# Revit family: Sink-Kitchen-KOHLER-Undertone-K-3188
name_source: partatom
category: Plumbing Fixtures
revit_build: Autodesk Revit 2015 (Build: 20140606_1530(x64)
units: mm (PartAtom-declared; Revit-internal decimal feet)

## types (1)
- NA-Stainless
    ADA Compliant = No
    Assembly Code = D2010400
    Date Modified = 09/19/2017
    Default Elevation = 35"
    Description = Undertone 43inch x 8-1/4inch x 6-5/16inch under-mount single-bowl trough kitchen sink
    Finish = Kohler-Metal-NA-Stainless
    Flow Rate = 0 GPM
    Height = 8 7/8"
    Inlet Connector = Inlet Connection
    Length = 43"
    Manufacturer = KOHLER Co.
    MasterFormat 1995 = 15410
    MasterFormat 2004 = 22.41.16
    Material = 16-Gauge Stainless Steel
    Model = K-3188-NA
    Outlet Connector = Outlet Connection
    Pressure = 0.00 psi
    Product Documentation Link = http://www.us.kohler.com
    Product Name = Undertone
    Product Page URL = http://www.us.kohler.com
    Type = 0
    URL = http://www.us.kohler.com
    Waste Connection = Yes
    Width = 8 1/4"

## geometry (parser evidence)
native form markers: Blend x2, Sweep x6
no freeform markers — native parametric forms only
